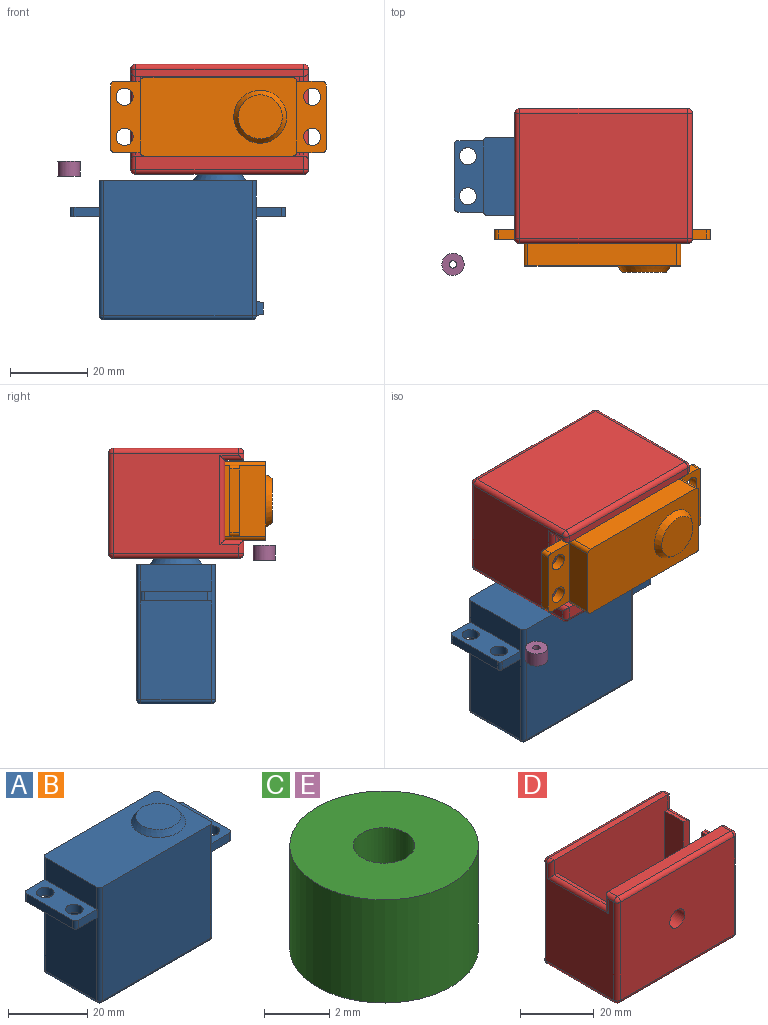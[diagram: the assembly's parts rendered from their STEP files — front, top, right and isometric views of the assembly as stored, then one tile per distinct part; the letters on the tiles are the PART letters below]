
ASSEMBLY  parts=5 mates=4
PART A: 45 faces, bbox 55.9x20.3x37.7 mm
  f0: plane 18.29x6.86mm, normal (-1,0,0), area 125.4mm2, adj f6,f21,f33,f38
  f1: plane 18.29x6.86mm, normal (1,0,0), area 125.4mm2, adj f6,f30,f35,f44
  f2: plane 25.65x18.29mm, normal (1,0,0), area 446.3mm2, adj f9,f10,f11,f12,f29,f35,f41,f44
  f3: plane 38.61x35.05mm, normal (0,-1,0), area 1353.3mm2, adj f6,f38,f42,f44
  f4: plane 38.61x35.05mm, normal (0,1,0), area 1353.3mm2, adj f6,f33,f35,f36
  f5: plane 25.65x18.29mm, normal (-1,0,0), area 469.2mm2, adj f20,f33,f37,f38
  f6: plane 40.64x20.32mm, normal (0,0,1), area 677.2mm2, adj f0,f1,f3,f4,f32,f33,f35,f38
  f7: plane 38.61x18.29mm, normal (0,0,-1), area 706.1mm2, adj f36,f37,f41,f42
  f8: plane 6.02x3.07mm, normal (1,0,0), area 18.5mm2, adj f9,f10,f11,f12
  f9: plane 6.35x1.91mm, normal (0.14,0,0.99), area 11.9mm2, adj f2,f8,f10,f12
  f10: plane 3.61x1.91mm, normal (0.09,-1,0), area 6.4mm2, adj f2,f8,f9,f11
  f11: plane 6.35x1.91mm, normal (0.14,0,-0.99), area 11.9mm2, adj f2,f8,f10,f12
  f12: plane 3.61x1.91mm, normal (0.09,1,0), area 6.4mm2, adj f2,f8,f9,f11
  f13: plane 6.61x2.54mm, normal (0,1,0), area 16.8mm2, adj f14,f20,f21,f33
  f14: cylinder r=1.02mm len=2.54mm, axis (0,0,1), area 4.1mm2, adj f13,f15,f20,f21
  f15: plane 16.51x2.54mm, normal (-1,0,0), area 41.9mm2, adj f14,f16,f20,f21
  f16: cylinder r=1.02mm len=2.54mm, axis (0,0,1), area 4.1mm2, adj f15,f18,f20,f21
  f17: cylinder r=2.22mm len=4.45mm, axis (0,0,1), area 35.5mm2, adj f20,f21
  f18: plane 6.61x2.54mm, normal (0,-1,0), area 16.8mm2, adj f16,f20,f21,f38
  f19: cylinder r=2.22mm len=4.45mm, axis (0,0,1), area 35.5mm2, adj f20,f21
  f20: plane 18.54x7.63mm, normal (0,0,-1), area 109.8mm2, adj f5,f13,f14,f15,f16,f17,f18,f19
  f21: plane 18.54x7.63mm, normal (0,0,1), area 109.8mm2, adj f0,f13,f14,f15,f16,f17,f18,f19
  f22: plane 6.61x2.54mm, normal (0,1,0), area 16.8mm2, adj f26,f29,f30,f35
  f23: plane 6.61x2.54mm, normal (0,-1,0), area 16.8mm2, adj f24,f29,f30,f44
  f24: cylinder r=1.02mm len=2.54mm, axis (0,0,1), area 4.1mm2, adj f23,f25,f29,f30
  f25: plane 16.51x2.54mm, normal (1,0,0), area 41.9mm2, adj f24,f26,f29,f30
  f26: cylinder r=1.02mm len=2.54mm, axis (0,0,1), area 4.1mm2, adj f22,f25,f29,f30
  f27: cylinder r=2.22mm len=4.45mm, axis (0,0,1), area 35.5mm2, adj f29,f30
  f28: cylinder r=2.22mm len=4.45mm, axis (0,0,1), area 35.5mm2, adj f29,f30
  f29: plane 18.54x7.63mm, normal (0,0,-1), area 109.8mm2, adj f2,f22,f23,f24,f25,f26,f27,f28
  f30: plane 18.54x7.63mm, normal (0,0,1), area 109.8mm2, adj f1,f22,f23,f24,f25,f26,f27,f28
  f31: plane 11.4x11.4mm, normal (0,0,1), area 102.2mm2, adj f32
  f32: cone r=6.86mm half-angle=35deg, axis (0,0,-1), area 79.5mm2, adj f6,f31
  f33: cylinder r=1.02mm len=35.05mm, axis (0,0,-1), area 55.6mm2, adj f0,f4,f5,f6,f13,f20,f21,f34
  f34: sphere r=1.02mm, area 1.6mm2, adj f33,f36,f37
  f35: cylinder r=1.02mm len=35.05mm, axis (0,0,1), area 55.6mm2, adj f1,f2,f4,f6,f22,f29,f30,f39
  f36: cylinder r=1.02mm len=38.61mm, axis (-1,0,0), area 61.6mm2, adj f4,f7,f34,f39
  f37: cylinder r=1.02mm len=18.29mm, axis (0,-1,0), area 29.2mm2, adj f5,f7,f34,f40
  f38: cylinder r=1.02mm len=35.05mm, axis (0,0,1), area 55.6mm2, adj f0,f3,f5,f6,f18,f20,f21,f40
  f39: sphere r=1.02mm, area 1.6mm2, adj f35,f36,f41
  f40: sphere r=1.02mm, area 1.6mm2, adj f37,f38,f42
  f41: cylinder r=1.02mm len=18.29mm, axis (0,1,0), area 29.2mm2, adj f2,f7,f39,f43
  f42: cylinder r=1.02mm len=38.61mm, axis (1,0,0), area 61.6mm2, adj f3,f7,f40,f43
  f43: sphere r=1.02mm, area 1.6mm2, adj f41,f42,f44
  f44: cylinder r=1.02mm len=35.05mm, axis (0,0,-1), area 55.6mm2, adj f1,f2,f3,f6,f23,f29,f30,f43
PART B: same geometry as A
PART C: 4 faces, bbox 5.8x5.8x3.9 mm
  f0: cylinder r=0.94mm len=3.86mm, axis (0,0,-1), area 22.8mm2, adj f2,f3
  f1: cylinder r=2.88mm len=5.77mm, axis (0,0,-1), area 69.9mm2, adj f2,f3
  f2: plane 5.77x5.77mm, normal (0,0,1), area 23.3mm2, adj f0,f1
  f3: plane 5.77x5.77mm, normal (0,0,-1), area 23.3mm2, adj f0,f1
PART D: 48 faces, bbox 46x28.6x35.1 mm
  f0: plane 7.14x1.11mm, normal (0,0,1), area 7.9mm2, adj f10,f15,f17,f19
  f1: plane 25.4x6.7mm, normal (-1,0,0), area 170.1mm2, adj f2,f8,f14,f16
  f2: plane 43.66x20.64mm, normal (0,0,1), area 868mm2, adj f1,f4,f8,f10,f13,f15,f16,f17
  f3: plane 43.5x32.51mm, normal (0,-1,0), area 1388.1mm2, adj f18,f37,f38,f42,f43
  f4: plane 32.51x26.04mm, normal (1,0,0), area 569mm2, adj f2,f16,f17,f19,f20,f22,f29,f36
  f5: plane 43.5x32.51mm, normal (0,1,0), area 1414.2mm2, adj f23,f24,f29,f30
  f6: plane 32.51x26.04mm, normal (-1,0,0), area 733.1mm2, adj f24,f25,f28,f31,f32,f35,f38,f39
  f7: plane 43.5x26.04mm, normal (0,0,-1), area 1132.5mm2, adj f30,f31,f36,f37
  f8: plane 43.5x30.29mm, normal (0,1,0), area 1235mm2, adj f1,f2,f9,f12,f13,f14,f18,f35
  f9: plane 43.5x3.49mm, normal (0,0,1), area 151.9mm2, adj f8,f39,f43,f45
  f10: plane 43.5x30.29mm, normal (0,-1,0), area 1261.1mm2, adj f0,f2,f11,f12,f13,f15,f20,f28
  f11: plane 43.5x1.91mm, normal (0,0,1), area 82.9mm2, adj f10,f22,f23,f25
  f12: plane 20.64x1.11mm, normal (0,0,1), area 22.9mm2, adj f8,f10,f13,f32
  f13: plane 25.4x20.64mm, normal (1,0,0), area 524.2mm2, adj f2,f8,f10,f12
  f14: plane 6.7x1.11mm, normal (0,0,1), area 7.4mm2, adj f1,f8,f16,f47
  f15: plane 25.4x7.14mm, normal (-1,0,0), area 181.3mm2, adj f0,f2,f10,f17
  f16: plane 25.4x2.38mm, normal (0,1,0), area 60.1mm2, adj f1,f2,f4,f14,f47
  f17: plane 25.4x2.38mm, normal (0,-1,0), area 60.1mm2, adj f0,f2,f4,f15,f19
  f18: cylinder r=2.88mm len=5.77mm, axis (0,-1,0), area 86.3mm2, adj f3,f8
  f19: cylinder r=1.27mm len=8.41mm, axis (0,-1,0), area 15.2mm2, adj f0,f4,f17,f20
  f20: cylinder r=1.27mm len=6.16mm, axis (0,0,-1), area 9.8mm2, adj f4,f10,f19,f22
  f21: sphere r=1.27mm, area 2.5mm2, adj f23,f24,f25
  f22: cylinder r=1.27mm len=1.91mm, axis (0,-1,0), area 2.9mm2, adj f4,f11,f20,f26
  f23: cylinder r=1.27mm len=43.5mm, axis (1,0,0), area 86.8mm2, adj f5,f11,f21,f26
  f24: cylinder r=1.27mm len=32.51mm, axis (0,0,-1), area 64.9mm2, adj f5,f6,f21,f27
  f25: cylinder r=1.27mm len=1.91mm, axis (0,1,0), area 2.9mm2, adj f6,f11,f21,f28
  f26: sphere r=1.27mm, area 2.5mm2, adj f22,f23,f29
  f27: sphere r=1.27mm, area 2.5mm2, adj f24,f30,f31
  f28: cylinder r=1.27mm len=6.16mm, axis (0,0,1), area 9.8mm2, adj f6,f10,f25,f32
  f29: cylinder r=1.27mm len=32.51mm, axis (0,0,1), area 64.9mm2, adj f4,f5,f26,f33
  f30: cylinder r=1.27mm len=43.5mm, axis (-1,0,0), area 86.8mm2, adj f5,f7,f27,f33
  f31: cylinder r=1.27mm len=26.04mm, axis (0,-1,0), area 51.9mm2, adj f6,f7,f27,f34
  f32: cylinder r=1.27mm len=23.18mm, axis (0,1,0), area 43mm2, adj f6,f12,f28,f35
  f33: sphere r=1.27mm, area 2.5mm2, adj f29,f30,f36
  f34: sphere r=1.27mm, area 2.5mm2, adj f31,f37,f38
  f35: cylinder r=1.27mm len=6.16mm, axis (0,0,-1), area 9.8mm2, adj f6,f8,f32,f39
  f36: cylinder r=1.27mm len=26.04mm, axis (0,1,0), area 51.9mm2, adj f4,f7,f33,f40
  f37: cylinder r=1.27mm len=43.5mm, axis (1,0,0), area 86.8mm2, adj f3,f7,f34,f40
  f38: cylinder r=1.27mm len=32.51mm, axis (0,0,1), area 64.9mm2, adj f3,f6,f34,f41
  f39: cylinder r=1.27mm len=3.49mm, axis (0,1,0), area 6mm2, adj f6,f9,f35,f41
  f40: sphere r=1.27mm, area 2.5mm2, adj f36,f37,f42
  f41: sphere r=1.27mm, area 2.5mm2, adj f38,f39,f43
  f42: cylinder r=1.27mm len=32.51mm, axis (0,0,-1), area 64.9mm2, adj f3,f4,f40,f44
  f43: cylinder r=1.27mm len=43.5mm, axis (-1,0,0), area 86.8mm2, adj f3,f9,f41,f44
  f44: sphere r=1.27mm, area 2.5mm2, adj f42,f43,f45
  f45: cylinder r=1.27mm len=3.49mm, axis (0,-1,0), area 6mm2, adj f4,f9,f44,f46
  f46: cylinder r=1.27mm len=6.16mm, axis (0,0,1), area 9.8mm2, adj f4,f8,f45,f47
  f47: cylinder r=1.27mm len=7.97mm, axis (0,-1,0), area 14.3mm2, adj f4,f14,f16,f46
PART E: same geometry as C
PLACE A t=(5.07,14.67,-3.17)mm fixed
PLACE B rot(axis=(1,0,0),90deg) t=(15.6,27.44,49.47)mm
PLACE C t=(5.07,14.67,-3.17)mm
PLACE D rot(axis=(1,0,0),90deg) t=(15.91,32.2,48.84)mm
PLACE E t=(-34,-8.21,-3.66)mm
MATE planar B.f5 <-> D.f13  axis (-1,0,0) through (-4.72,13.59,49.47)mm
MATE revolute A.f32 <-> C.f0  axis (0,0,1) through (15.91,14.67,34.55)mm
MATE planar B.f7 <-> D.f2  axis (0,1,0) through (15.6,27.44,49.47)mm
MATE planar B.f3 <-> D.f8  axis (0,0,-1) through (15.6,8.9,39.31)mm
